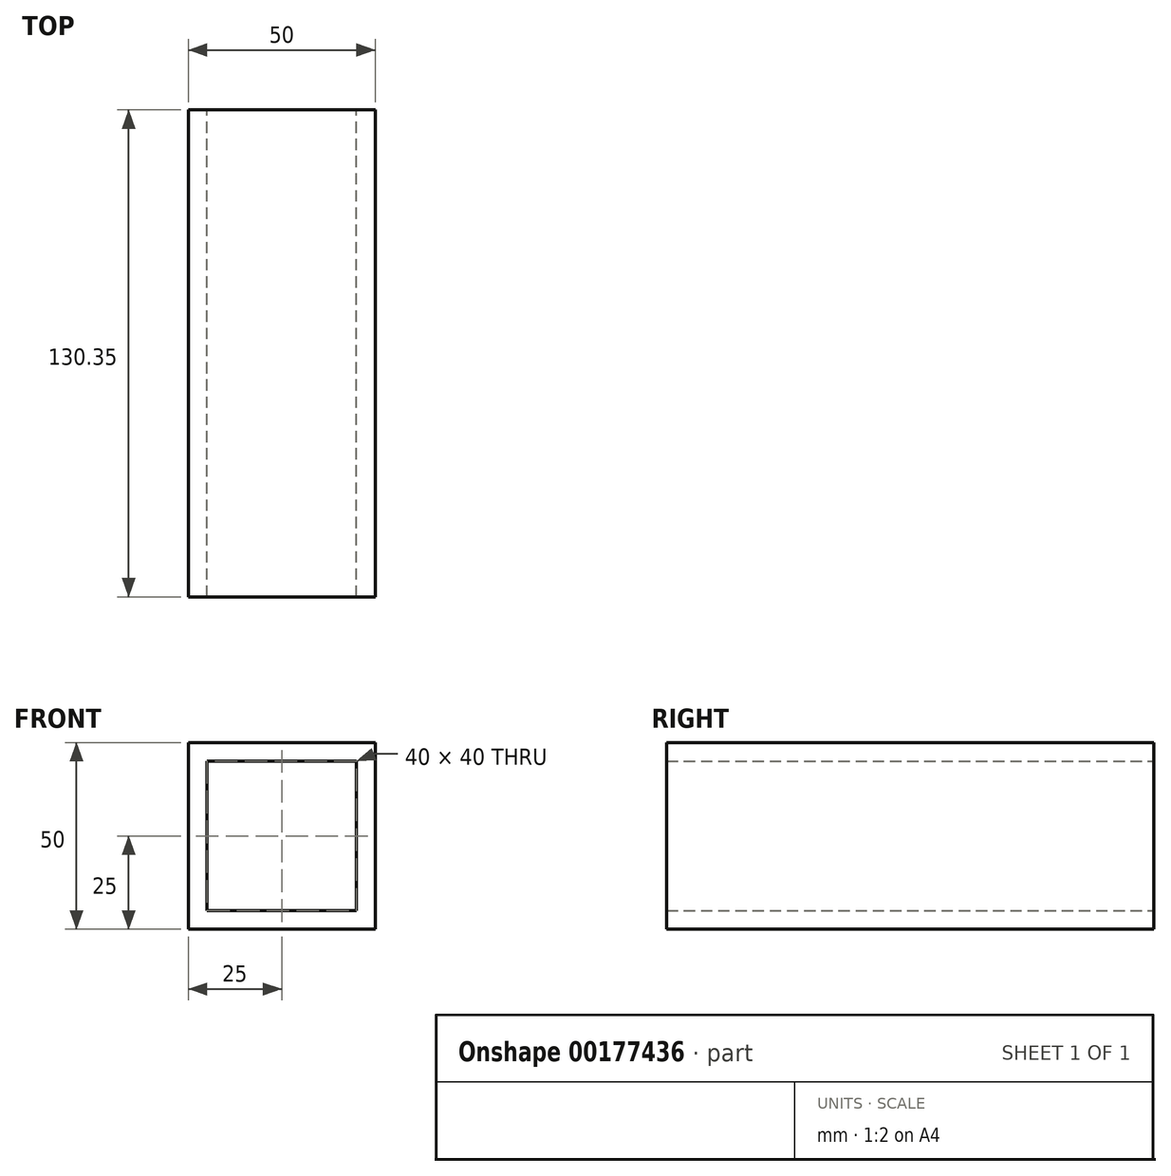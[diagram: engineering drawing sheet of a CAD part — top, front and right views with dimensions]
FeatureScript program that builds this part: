
annotation { "Feature Type Name" : "Feature", "Feature Type Description" : "" }
export const myFeature = defineFeature(function(context is Context, id is Id, definition is map)
    precondition{}
    {
        {
            var Q0;
            Q0=qCreatedBy(makeId("Front.planeOp"),FACE);
            var sketch = newSketch(context, id + "F0", { "sketchPlane" : qUnion([Q0])});
            skLineSegment(sketch, "E0.bottom", {"start": v(25, -25) * mm, "end": v(-25, -25) * mm});
            skLineSegment(sketch, "E0.top", {"start": v(25, 25) * mm, "end": v(-25, 25) * mm});
            skLineSegment(sketch, "E0.left", {"start": v(25, -25) * mm, "end": v(25, 25) * mm});
            skLineSegment(sketch, "E0.right", {"start": v(-25, -25) * mm, "end": v(-25, 25) * mm});
            skPoint(sketch, "E0.middle", {"position": v(0, 0) * mm});
            skLineSegment(sketch, "E1.0", {"start": v(20, 20) * mm, "end": v(-20, 20) * mm});
            skLineSegment(sketch, "E1.1", {"start": v(20, -20) * mm, "end": v(20, 20) * mm});
            skLineSegment(sketch, "E1.2", {"start": v(20, -20) * mm, "end": v(-20, -20) * mm});
            skLineSegment(sketch, "E1.3", {"start": v(-20, -20) * mm, "end": v(-20, 20) * mm});
            skSolve(sketch);
        }
        {
            var Q0;
            Q0=makeQuery(id+"F0.imprint","IMPRINT",FACE,{"disambiguationData":[TD([[makeQuery(id+"F0.imprint","IMPRINT",EDGE,{"derivedFrom":sQuery(id+"F0.wireOp",EDGE,"E0.bottom")}),-1.0]])]});
            extrude(context, id + "F1", {"entities" : qUnion([Q0]), "depth" : 130.35 * mm});
        }
    });
